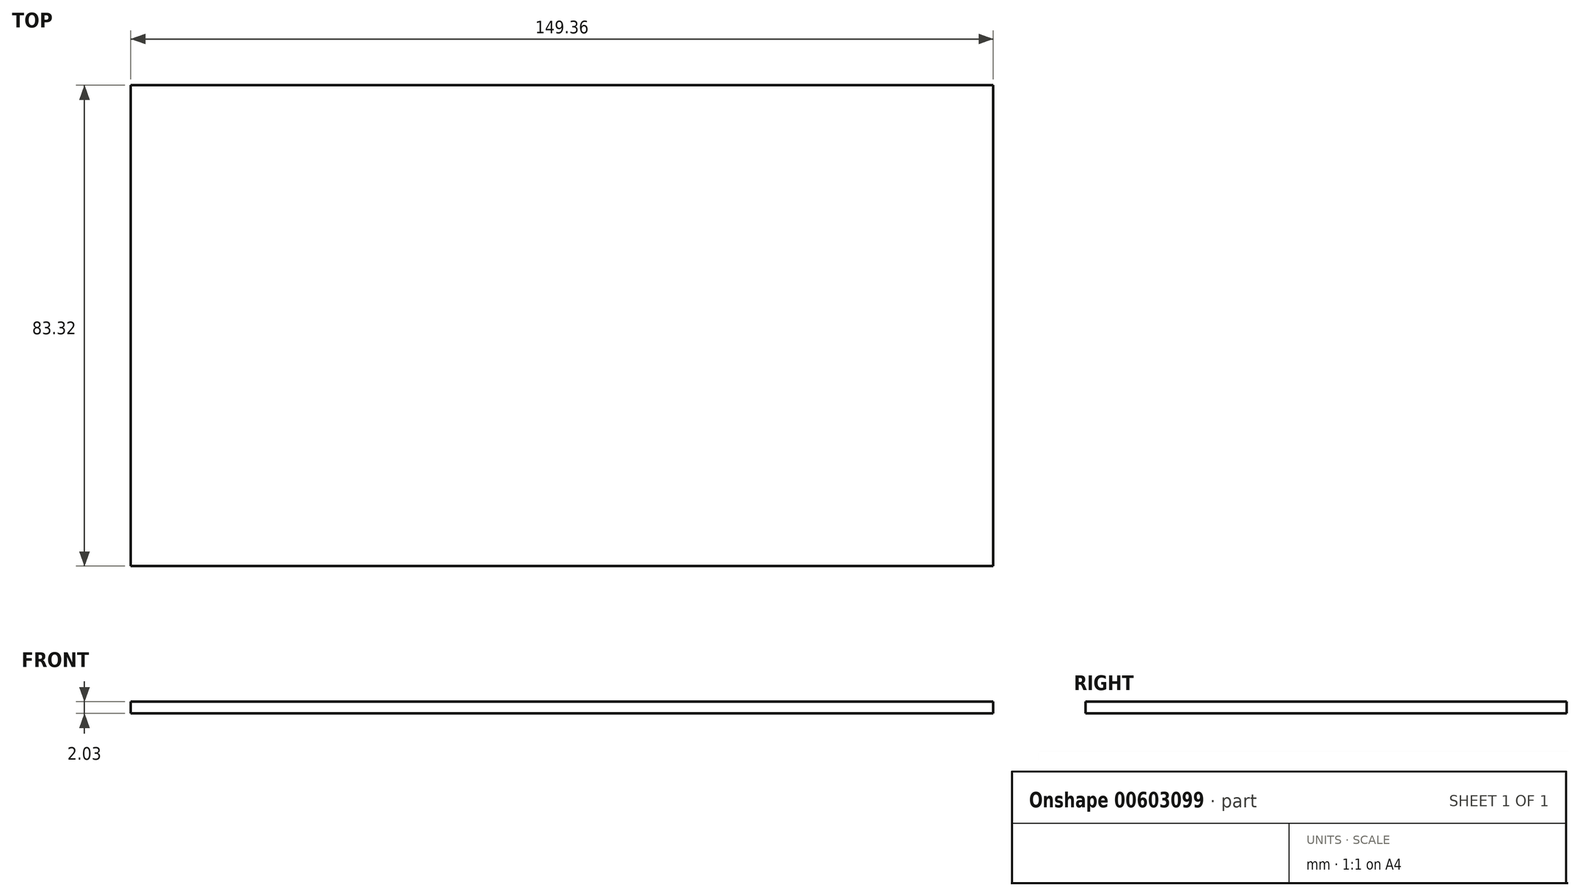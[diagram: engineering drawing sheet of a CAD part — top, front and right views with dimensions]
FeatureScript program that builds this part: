
annotation { "Feature Type Name" : "Feature", "Feature Type Description" : "" }
export const myFeature = defineFeature(function(context is Context, id is Id, definition is map)
    precondition{}
    {
        {
            var Q0;
            Q0=qCreatedBy(makeId("Top.planeOp"),FACE);
            var sketch = newSketch(context, id + "F0", { "sketchPlane" : qUnion([Q0])});
            skLineSegment(sketch, "E0.bottom", {"start": v(74.68, 41.66) * mm, "end": v(-74.68, 41.66) * mm});
            skLineSegment(sketch, "E0.top", {"start": v(74.68, -41.66) * mm, "end": v(-74.68, -41.66) * mm});
            skLineSegment(sketch, "E0.left", {"start": v(74.68, 41.66) * mm, "end": v(74.68, -41.66) * mm});
            skLineSegment(sketch, "E0.right", {"start": v(-74.68, 41.66) * mm, "end": v(-74.68, -41.66) * mm});
            skPoint(sketch, "E0.middle", {"position": v(0, 0) * mm});
            skSolve(sketch);
        }
        {
            var Q0;
            Q0 = qSketchRegion(id + "F0", true);
            extrude(context, id + "F1", {"entities" : qUnion([Q0]), "depth" : 2.03 * mm, "offsetDistance" : 25.4 * mm});
        }
    });
